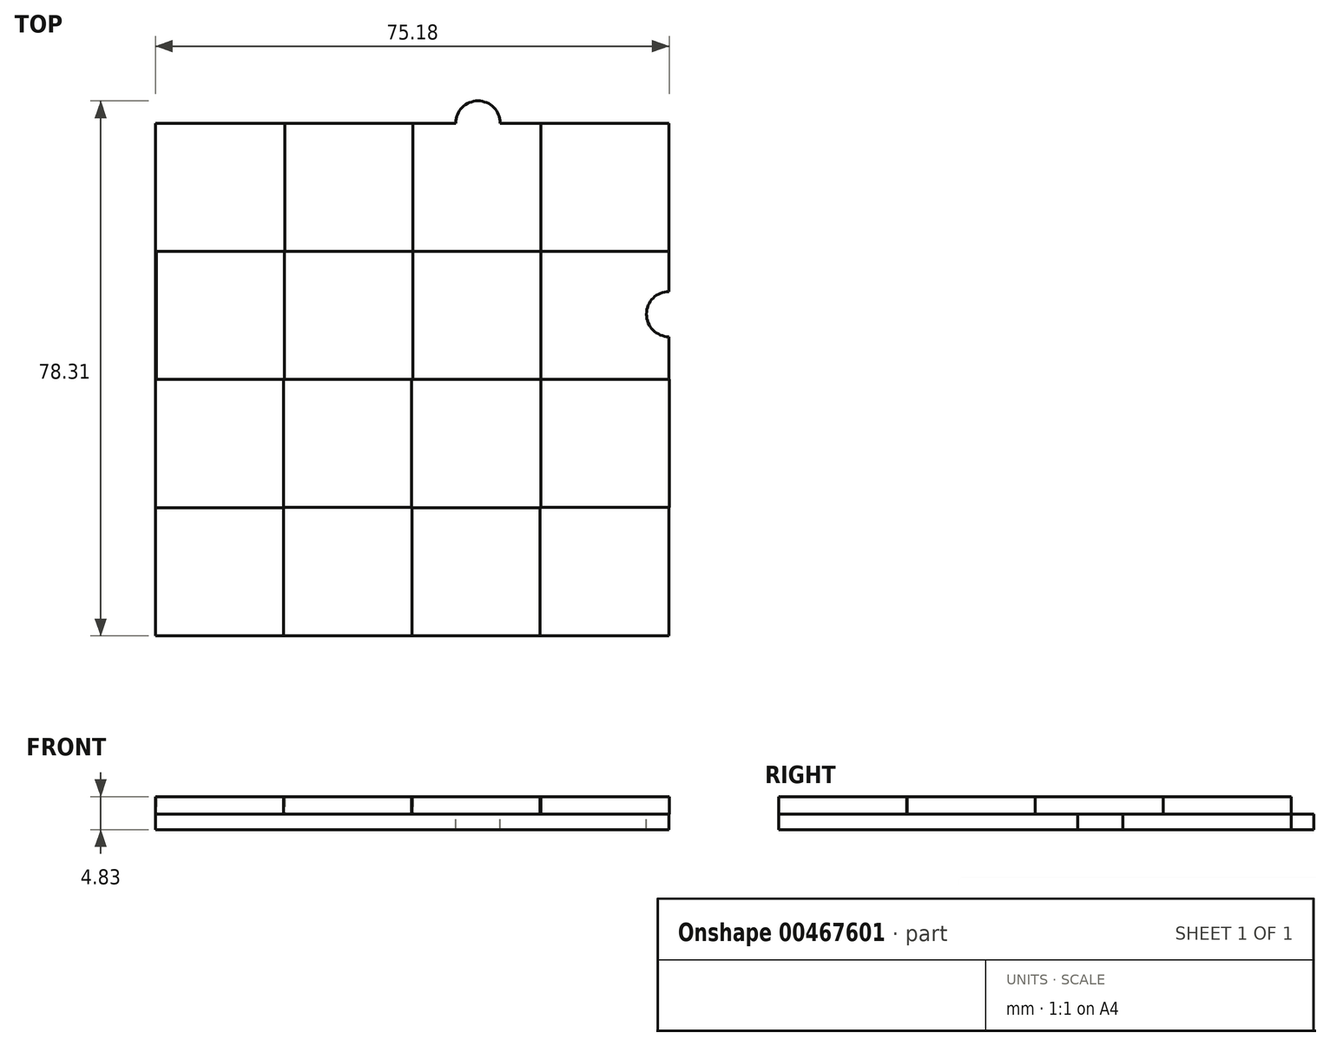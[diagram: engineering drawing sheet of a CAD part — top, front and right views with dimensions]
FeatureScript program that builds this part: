
annotation { "Feature Type Name" : "Feature", "Feature Type Description" : "" }
export const myFeature = defineFeature(function(context is Context, id is Id, definition is map)
    precondition{}
    {
        {
            var Q0;
            Q0=qCreatedBy(makeId("Top.planeOp"),FACE);
            var sketch = newSketch(context, id + "F0", { "sketchPlane" : qUnion([Q0])});
            skLineSegment(sketch, "E0.bottom", {"start": v(-49.27, 48.56) * mm, "end": v(-30.54, 48.56) * mm});
            skLineSegment(sketch, "E0.top", {"start": v(-49.27, 29.83) * mm, "end": v(-30.54, 29.83) * mm});
            skLineSegment(sketch, "E0.left", {"start": v(-49.27, 48.56) * mm, "end": v(-49.27, 29.83) * mm});
            skLineSegment(sketch, "E0.right", {"start": v(-30.54, 48.56) * mm, "end": v(-30.54, 29.83) * mm});
            skLineSegment(sketch, "E1.bottom", {"start": v(-30.52, 29.87) * mm, "end": v(-11.79, 29.87) * mm});
            skLineSegment(sketch, "E1.top", {"start": v(-30.52, 11.14) * mm, "end": v(-11.79, 11.14) * mm});
            skLineSegment(sketch, "E1.left", {"start": v(-30.52, 29.87) * mm, "end": v(-30.52, 11.14) * mm});
            skLineSegment(sketch, "E1.right", {"start": v(-11.79, 29.87) * mm, "end": v(-11.79, 11.14) * mm});
            skLineSegment(sketch, "E2.bottom", {"start": v(-11.76, 11.11) * mm, "end": v(6.98, 11.11) * mm});
            skLineSegment(sketch, "E2.top", {"start": v(-11.76, -7.62) * mm, "end": v(6.98, -7.62) * mm});
            skLineSegment(sketch, "E2.left", {"start": v(-11.76, 11.11) * mm, "end": v(-11.76, -7.62) * mm});
            skLineSegment(sketch, "E2.right", {"start": v(6.98, 11.11) * mm, "end": v(6.98, -7.62) * mm});
            skLineSegment(sketch, "E3.bottom", {"start": v(-49.43, 11.11) * mm, "end": v(-30.7, 11.11) * mm});
            skLineSegment(sketch, "E3.top", {"start": v(-49.43, -7.62) * mm, "end": v(-30.7, -7.62) * mm});
            skLineSegment(sketch, "E3.left", {"start": v(-49.43, 11.11) * mm, "end": v(-49.43, -7.62) * mm});
            skLineSegment(sketch, "E3.right", {"start": v(-30.7, 11.11) * mm, "end": v(-30.7, -7.62) * mm});
            skLineSegment(sketch, "E4.bottom", {"start": v(-68.06, 29.83) * mm, "end": v(-49.32, 29.83) * mm});
            skLineSegment(sketch, "E4.top", {"start": v(-68.06, 11.1) * mm, "end": v(-49.32, 11.1) * mm});
            skLineSegment(sketch, "E4.left", {"start": v(-68.06, 29.83) * mm, "end": v(-68.06, 11.1) * mm});
            skLineSegment(sketch, "E4.right", {"start": v(-49.32, 29.83) * mm, "end": v(-49.32, 11.1) * mm});
            skLineSegment(sketch, "E5.bottom", {"start": v(-11.79, 48.6) * mm, "end": v(6.94, 48.6) * mm});
            skLineSegment(sketch, "E5.top", {"start": v(-11.79, 29.87) * mm, "end": v(6.94, 29.87) * mm});
            skLineSegment(sketch, "E5.left", {"start": v(-11.79, 48.6) * mm, "end": v(-11.79, 29.87) * mm});
            skLineSegment(sketch, "E5.right", {"start": v(6.94, 48.6) * mm, "end": v(6.94, 29.87) * mm});
            skLineSegment(sketch, "E6.bottom", {"start": v(-30.63, -7.7) * mm, "end": v(-11.9, -7.7) * mm});
            skLineSegment(sketch, "E6.top", {"start": v(-30.63, -26.44) * mm, "end": v(-11.9, -26.44) * mm});
            skLineSegment(sketch, "E6.left", {"start": v(-30.63, -7.7) * mm, "end": v(-30.63, -26.44) * mm});
            skLineSegment(sketch, "E6.right", {"start": v(-11.9, -7.7) * mm, "end": v(-11.9, -26.44) * mm});
            skLineSegment(sketch, "E7.bottom", {"start": v(-68.2, -7.7) * mm, "end": v(-49.47, -7.7) * mm});
            skLineSegment(sketch, "E7.top", {"start": v(-68.2, -26.44) * mm, "end": v(-49.47, -26.44) * mm});
            skLineSegment(sketch, "E7.left", {"start": v(-68.2, -7.7) * mm, "end": v(-68.2, -26.44) * mm});
            skLineSegment(sketch, "E7.right", {"start": v(-49.47, -7.7) * mm, "end": v(-49.47, -26.44) * mm});
            skSolve(sketch);
        }
        {
            var Q0;
            Q0=makeQuery(id+"F0.imprint","IMPRINT",FACE,{"disambiguationData":[TD([[makeQuery(id+"F0.imprint","IMPRINT",EDGE,{"derivedFrom":sQuery(id+"F0.wireOp",EDGE,"E5.bottom")}),-1.0]])]});
            var Q1;
            Q1=makeQuery(id+"F0.imprint","IMPRINT",FACE,{"disambiguationData":[TD([[makeQuery(id+"F0.imprint","IMPRINT",EDGE,{"derivedFrom":sQuery(id+"F0.wireOp",EDGE,"E6.bottom")}),-1.0]])]});
            var Q2;
            Q2=makeQuery(id+"F0.imprint","IMPRINT",FACE,{"disambiguationData":[TD([[makeQuery(id+"F0.imprint","IMPRINT",EDGE,{"derivedFrom":sQuery(id+"F0.wireOp",EDGE,"E7.bottom")}),-1.0]])]});
            var Q3;
            {var subQ4=sQuery(id+"F0.wireOp",EDGE,"E4.bottom");Q3=makeQuery(id+"F0.imprint","IMPRINT",FACE,{"disambiguationData":[TD([[makeQuery(id+"F0.imprint","IMPRINT",EDGE,{"derivedFrom":subQ4}),-1.0]])]});}
            var Q4;
            {var subQ2=sQuery(id+"F0.wireOp",EDGE,"E3.top");Q4=makeQuery(id+"F0.imprint","IMPRINT",FACE,{"disambiguationData":[TD([[makeQuery(id+"F0.imprint","IMPRINT",EDGE,{"derivedFrom":subQ2}),1.0]])]});}
            var Q5;
            Q5=makeQuery(id+"F0.imprint","IMPRINT",FACE,{"disambiguationData":[TD([[makeQuery(id+"F0.imprint","IMPRINT",EDGE,{"derivedFrom":sQuery(id+"F0.wireOp",EDGE,"E2.bottom")}),-1.0]])]});
            var Q6;
            Q6=makeQuery(id+"F0.imprint","IMPRINT",FACE,{"disambiguationData":[TD([[makeQuery(id+"F0.imprint","IMPRINT",EDGE,{"derivedFrom":sQuery(id+"F0.wireOp",EDGE,"E0.bottom")}),-1.0]])]});
            var Q7;
            Q7=makeQuery(id+"F0.imprint","IMPRINT",FACE,{"disambiguationData":[TD([[makeQuery(id+"F0.imprint","IMPRINT",EDGE,{"derivedFrom":sQuery(id+"F0.wireOp",EDGE,"E1.bottom")}),-1.0]])]});
            var Q8;
            {var subQ0=sQuery(id+"F0.wireOp",EDGE,"E3.left");var subQ1=sQuery(id+"F0.wireOp",EDGE,"E3.bottom");var subQ2=makeQuery(id+"F0.imprint","INTERSECT",VERTEX,{"derivedFrom":[subQ1,subQ0]});Q8=makeQuery(id+"F0.imprint","IMPRINT",FACE,{"disambiguationData":[TD([[makeQuery(id+"F0.imprint","IMPRINT",EDGE,{"disambiguationData":[TD([[subQ2,-1.0]])],"derivedFrom":subQ1}),-1.0]])]});}
            extrude(context, id + "F1", {"entities" : qUnion([Q0, Q1, Q2, Q3, Q4, Q5, Q6, Q7, Q8]), "depth" : 2.54 * mm});
        }
        {
            var Q0;
            Q0=qCreatedBy(makeId("Top.planeOp"),FACE);
            var sketch = newSketch(context, id + "F2", { "sketchPlane" : qUnion([Q0])});
            skLineSegment(sketch, "E8.bottom", {"start": v(-68.19, 48.6) * mm, "end": v(6.97, 48.6) * mm});
            skLineSegment(sketch, "E8.top", {"start": v(-68.19, -26.43) * mm, "end": v(6.97, -26.43) * mm});
            skLineSegment(sketch, "E8.left", {"start": v(-68.19, 48.6) * mm, "end": v(-68.19, -26.43) * mm});
            skLineSegment(sketch, "E8.right", {"start": v(6.97, 48.6) * mm, "end": v(6.97, -26.43) * mm});
            skSolve(sketch);
        }
        {
            var Q0;
            Q0 = qSketchRegion(id + "F2", true);
            extrude(context, id + "F3", {"entities" : qUnion([Q0]), "oppositeDirection" : true, "depth" : 2.3 * mm});
        }
        {
            var Q0;
            Q0=makeQuery(id+"F3.opExtrude","CAP_FACE",FACE,{"disambiguationData":[OSD([sQuery(id+"F2.wireOp",EDGE,"E8.bottom"),sQuery(id+"F2.wireOp",EDGE,"E8.top"),sQuery(id+"F2.wireOp",EDGE,"E8.left"),sQuery(id+"F2.wireOp",EDGE,"E8.right")])],"isStart":true});
            var sketch = newSketch(context, id + "F4", { "sketchPlane" : qUnion([Q0])});
            skCircle(sketch, "E9", {"center": v(6.97, 20.66) * mm, "radius": 3.31 * mm});
            skCircle(sketch, "E10", {"center": v(-21, 48.6) * mm, "radius": 3.26 * mm});
            skSolve(sketch);
        }
        {
            var Q0;
            {var subQ0=sQuery(id+"F4.wireOp",EDGE,"E9");var subQ1=makeQuery(id+"F3.opExtrude","CAP_EDGE",EDGE,{"disambiguationData":[OSD([sQuery(id+"F2.wireOp",EDGE,"E8.right")])],"isStart":true});var subQ2=makeQuery(id+"F4.imprint","INTERSECT",VERTEX,{"disambiguationData":[OD(0.0)],"derivedFrom":[subQ1,subQ0]});Q0=makeQuery(id+"F4.imprint","IMPRINT",FACE,{"disambiguationData":[TD([[makeQuery(id+"F4.imprint","IMPRINT",EDGE,{"disambiguationData":[TD([[subQ2,-1.0]])],"derivedFrom":subQ0}),1.0]])]});}
            extrude(context, id + "F5", {"entities" : qUnion([Q0]), "operationType" : NewBodyOperationType.REMOVE, "oppositeDirection" : true, "depth" : 25.4 * mm});
        }
        {
            var Q0;
            {var subQ0=sQuery(id+"F4.wireOp",EDGE,"E10");var subQ1=makeQuery(id+"F3.opExtrude","CAP_EDGE",EDGE,{"disambiguationData":[OSD([sQuery(id+"F2.wireOp",EDGE,"E8.bottom")])],"isStart":true});var subQ2=makeQuery(id+"F4.imprint","INTERSECT",VERTEX,{"disambiguationData":[OD(0.0)],"derivedFrom":[subQ1,subQ0]});Q0=makeQuery(id+"F4.imprint","IMPRINT",FACE,{"disambiguationData":[TD([[makeQuery(id+"F4.imprint","IMPRINT",EDGE,{"disambiguationData":[TD([[subQ2,1.0]])],"derivedFrom":subQ0}),1.0]])]});}
            extrude(context, id + "F6", {"entities" : qUnion([Q0]), "operationType" : NewBodyOperationType.ADD, "oppositeDirection" : true, "depth" : 2.3 * mm});
        }
    });
